# Revit family: MixerSet_Wall_Abey_PocoP_BasinBath_FaceBased
name_source: partatom
category: Plumbing Fixtures
units: mm (PartAtom-declared; Revit-internal decimal feet)

## family parameters
Cut with Voids When Loaded = No
Host = Face
Maintain Annotation Orientation = No
OmniClass Number = 23.31.11.19
OmniClass Title = Faucet Mixing Valves
Part Type = Normal
Room Calculation Point = No
Round Connector Dimension = Use Diameter
Shared = No

## types (6) — shared parameters
Assembly Code = C1030210
CW Connection = Yes
Default Elevation = 0 mm
HW Connection = Yes
IfcExportAs = ifcValve
IfcExportType = FAUCET
Manufacturer = Abey
ManufacturerOverallHeight = 100 mm
ManufacturerOverallWidth = 180 mm
ManufacturerURLProductSpecific = https://www.abeyspecifier.com.au
ModifiedIssue = 20251103 $
URL = https://www.abey.com.au
Uniclass2015Code = Pr_40_20_87_55
Uniclass2015Title = Mixer taps
Uniclass2015Version = Products v1.38
Vent Connection = No
Waste Connection = No
zero-valued in all types: Cost

## per-type parameters (varying)
| type | BodyMaterial | Description | ManufacturerOverallDepth | ManufacturerSpecCode | Model | Type Comments |
| 220mm Gun Metal (8WS-EXT220-GM-LF) | Metal_Abey_GunMetal | Poco P Wall Basin/Bath Set 220mm | 234.5 mm | 8WS-EXT220-GM-LF | 8WS-EXT220-GM-LF | Mixer Set - Wall - Gun Metal |
| 220mm Brushed Nickel (8WS-EXT220-BN-LF) | Metal_Abey_BrushedNickel | Poco P Wall Basin/Bath Set 220mm | 234.5 mm | 8WS-EXT220-BN-LF | 8WS-EXT220-BN-LF | Mixer Set - Wall - Brushed Nickel |
| 220mm Brushed Brass (8WS-EXT220-BB-LF) | Metal_Abey_Brass | Poco P Wall Basin/Bath Set 220mm | 234.5 mm | 8WS-EXT220-BB-LF | 8WS-EXT220-BB-LF | Mixer Set - Wall - Brushed Brass |
| 165mm Gun Metal (8WS-EXT165-GM-LF) | Metal_Abey_GunMetal | Poco P Wall Basin/Bath Set 165mm | 179.5 mm | 8WS-EXT165-GM-LF | 8WS-EXT165-GM-LF | Mixer Set - Wall - Gun Metal |
| 165mm Brushed Nickel (8WS-EXT165-BN-LF) | Metal_Abey_BrushedNickel | Poco P Wall Basin/Bath Set 165mm | 179.5 mm | 8WS-EXT165-BN-LF | 8WS-EXT165-BN-LF | Mixer Set - Wall - Brushed Nickel |
| 165mm Brushed Brass (8WS-EXT165-BB-LF) | Metal_Abey_Brass | Poco P Wall Basin/Bath Set 165mm | 179.5 mm | 8WS-EXT165-BB-LF | 8WS-EXT165-BB-LF | Mixer Set - Wall - Brushed Brass |

## geometry (parser evidence)
native form markers: Sweep x4
no freeform markers — native parametric forms only
